# Revit family: Graypants_Scraplights_Classics_Moon_10_14_18_24_32_Pendant_R21_0925
name_source: partatom
category: Lighting Fixtures
units: mm (PartAtom-declared; Revit-internal decimal feet)

## family parameters
Cut with Voids When Loaded = No
Host = Face
Light Source = Yes
Part Type = Normal
Room Calculation Point = No
Round Connector Dimension = Use Diameter
Shared = No

## types (5) — shared parameters
Color Filter = 16777215
Default Elevation = 4' - 0"
Dimming Lamp Color Temperature Shift = <None>
Graypants_Cord/Canopy_Finish_Options = Black | White
Graypants_Manufacturer = Graypants
Graypants_Shade_Finish_Options = Natural Cardboard | Blonde Cardboard | White Cardboard
Graypants_URL = www.graypants.com

## per-type parameters (varying)
| type | Graypants_Model | Graypants_Moon10_Canopy_Visible | Graypants_Moon10_Cord_Visible | Graypants_Moon10_Shade_Visible | Graypants_Moon14_Canopy_Visible | Graypants_Moon14_Cord_Visible | Graypants_Moon14_Shade_Visible | Graypants_Moon18_Canopy_Visible | Graypants_Moon18_Cord_Visible | Graypants_Moon18_Shade_Visible | Graypants_Moon24_Canopy_Visible | Graypants_Moon24_Cord_Visible | Graypants_Moon24_Shade_Visible | Graypants_Moon32_Canopy_Visible | Graypants_Moon32_Cord_Visible | Graypants_Moon32_Shade_Visible | Light Source Symbol Size |
| Graypants_Scraplights_Moon10_(10" diameter)_Pendant | Scraplights_Classics_Moon_10 | Yes | Yes | Yes | No | No | No | No | No | No | No | No | No | No | No | No | 0' - 8 21/32" |
| Graypants_Scraplights_Moon14_(14" diameter)_Pendant | Scraplights_Classics_Moon_14 | No | No | No | Yes | Yes | Yes | No | No | No | No | No | No | No | No | No | 1' - 0 9/32" |
| Graypants_Scraplights_Moon18_(18" diameter)_Pendant | Scraplights_Classics_Moon_18 | No | No | No | No | No | No | Yes | Yes | Yes | No | No | No | No | No | No | 1' - 3 3/8" |
| Graypants_Scraplights_Moon24_(24" diameter)_Pendant | Scraplights_Classics_Moon_24 | No | No | No | No | No | No | No | No | No | Yes | Yes | Yes | No | No | No | 1' - 9 17/32" |
| Graypants_Scraplights_Moon32_(32" diameter)_Pendant | Scraplights_Classics_Moon_32 | No | No | No | No | No | No | No | No | No | No | No | No | Yes | Yes | Yes | 2' - 8" |

## geometry (parser evidence)
native form markers: Sweep x17
no freeform markers — native parametric forms only
